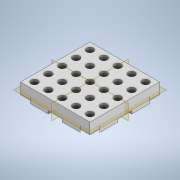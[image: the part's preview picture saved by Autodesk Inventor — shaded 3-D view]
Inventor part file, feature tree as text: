
AUTODESK INVENTOR PART (.ipt)
format: ipt  version: 2022.4 (Build 264492010, 492A)  size: 270,848 bytes
history: native  units: mm
features: extrude x4, sketch x3
ambient origin geometry x8: Origin, YZ Plane, XZ Plane, XY Plane, X Axis, Y Axis, Z Axis, Center Point
bodies: Solid1 (feature_tree)
feature tree (7):
  extrude  "Extrusion1"  Depth=50.0mm
  sketch  "Sketch2"  dims[d2=10.0mm d3=0.0mm d4=10.0mm]
  extrude  "Extrusion2"  Depth=10.0mm
  extrude  "Extrusion3"  Depth=3.0mm
  extrude  "Extrusion4"  Depth=40.0mm TaperAngle=360.0deg
  sketch  "Sketch1"  dims[d0=50.0mm d1=50.0mm]
  sketch  "Sketch3"  dims[d5=8.0mm d6=3.0mm d7=40.0mm d9=360.0deg d11=2.0mm d12=0.0mm d13=4.0mm d14=0.0mm d15=5.0mm d16=5.0mm d17=5.0mm d18=50.0mm d20=10.0mm d21=50.0mm d23=10.0mm d26=5.0mm d27=0.0mm d28=8.0mm d31=3.0mm d33=135.0deg d34=3.0mm d35=10.0mm d36=45.0deg d37=40.0mm d39=360.0deg]
